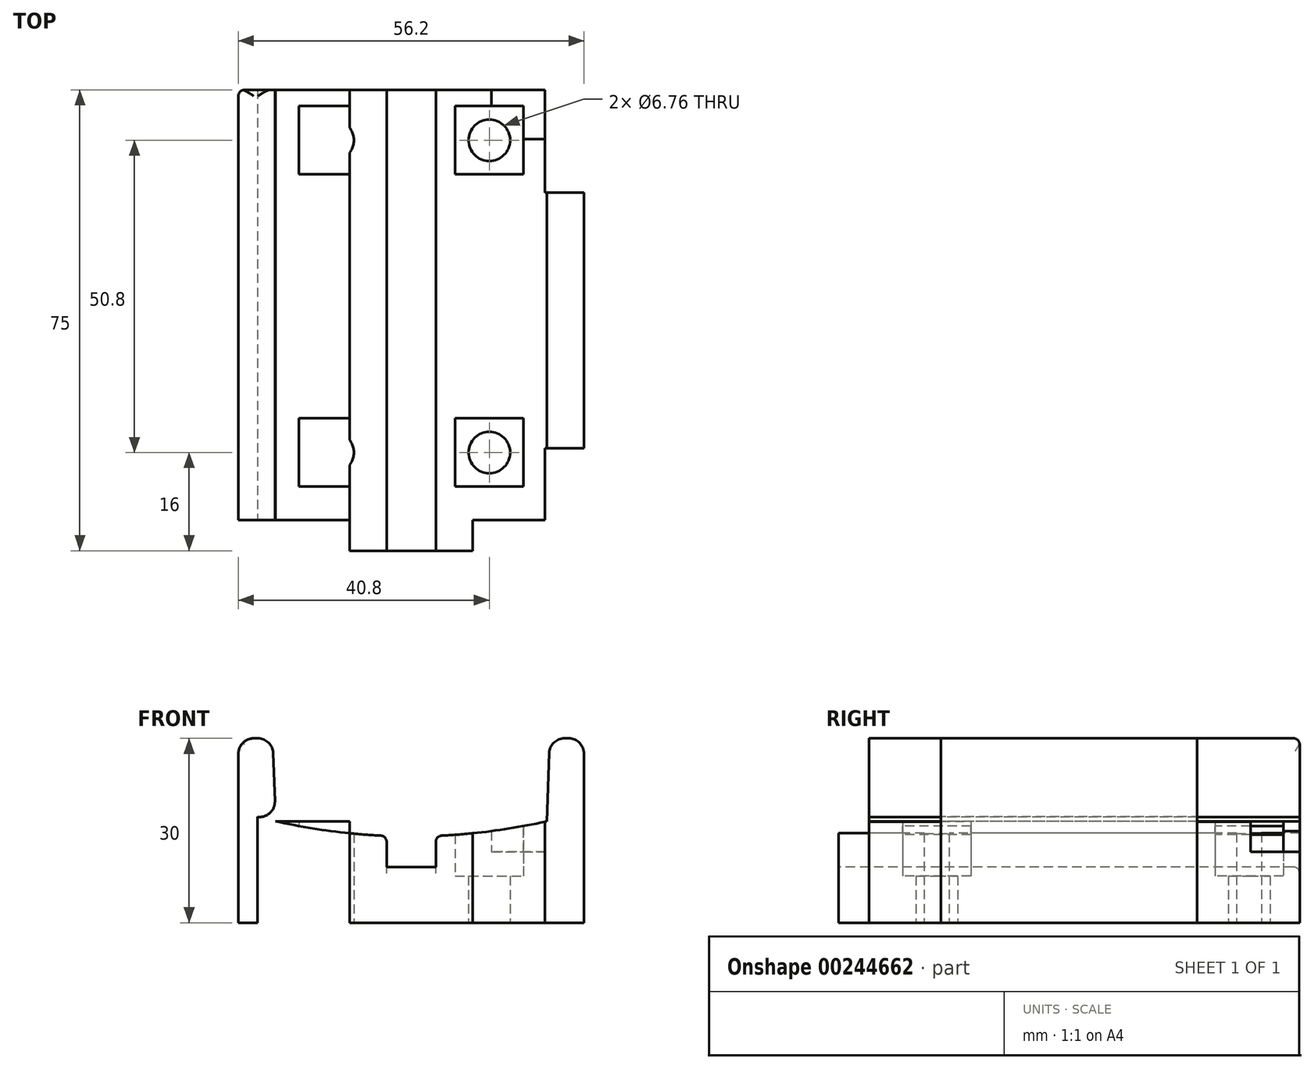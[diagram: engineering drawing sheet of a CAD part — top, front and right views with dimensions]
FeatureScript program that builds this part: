
annotation { "Feature Type Name" : "Feature", "Feature Type Description" : "" }
export const myFeature = defineFeature(function(context is Context, id is Id, definition is map)
    precondition{}
    {
        {
            var Q0;
            Q0=qCreatedBy(makeId("Front.planeOp"),FACE);
            var sketch = newSketch(context, id + "F0", { "sketchPlane" : qUnion([Q0])});
            skCircle(sketch, "E0", {"center": v(0, 0) * mm, "radius": 100.1 * mm});
            skLineSegment(sketch, "E1", {"start": v(0, 0) * mm, "end": v(0, -100.1) * mm});
            skLineSegment(sketch, "E2", {"start": v(0, -97.64) * mm, "end": v(22.05, -97.64) * mm});
            skLineSegment(sketch, "E3", {"start": v(0, -97.64) * mm, "end": v(-22.05, -97.64) * mm});
            skLineSegment(sketch, "E4", {"start": v(0, 0) * mm, "end": v(0, -27.77) * mm});
            skLineSegment(sketch, "E5", {"start": v(0, 0) * mm, "end": v(0, -84.15) * mm});
            skLineSegment(sketch, "E6", {"start": v(0, -84.15) * mm, "end": v(22.52, -84.15) * mm});
            skLineSegment(sketch, "E7", {"start": v(22.52, -84.15) * mm, "end": v(22.05, -97.64) * mm});
            skLineSegment(sketch, "E8", {"start": v(0, -84.15) * mm, "end": v(-22.52, -84.15) * mm});
            skLineSegment(sketch, "E9", {"start": v(-22.52, -84.15) * mm, "end": v(-22.05, -97.64) * mm});
            skLineSegment(sketch, "E10", {"start": v(-22.52, -84.15) * mm, "end": v(-28.1, -84.15) * mm});
            skLineSegment(sketch, "E11", {"start": v(-28.1, -84.15) * mm, "end": v(-28.1, -104.15) * mm});
            skLineSegment(sketch, "E12", {"start": v(-28.1, -104.15) * mm, "end": v(-48.1, -104.15) * mm});
            skLineSegment(sketch, "E13", {"start": v(-48.1, -104.15) * mm, "end": v(-48.1, -114.15) * mm});
            skLineSegment(sketch, "E14", {"start": v(-48.1, -114.15) * mm, "end": v(0, -114.15) * mm});
            skLineSegment(sketch, "E15", {"start": v(0, -114.15) * mm, "end": v(48.1, -114.15) * mm});
            skLineSegment(sketch, "E16", {"start": v(48.1, -114.15) * mm, "end": v(48.1, -104.15) * mm});
            skLineSegment(sketch, "E17", {"start": v(0, -97.64) * mm, "end": v(4, -97.64) * mm});
            skLineSegment(sketch, "E18", {"start": v(4, -105.1) * mm, "end": v(-4, -105.1) * mm});
            skLineSegment(sketch, "E19", {"start": v(-4, -105.1) * mm, "end": v(-4, -97.64) * mm});
            skLineSegment(sketch, "E20", {"start": v(4, -105.1) * mm, "end": v(4, -97.64) * mm});
            skLineSegment(sketch, "E21", {"start": v(22.05, -97.64) * mm, "end": v(13.05, -97.64) * mm});
            skLineSegment(sketch, "E22", {"start": v(13.05, -97.64) * mm, "end": v(13.05, -102.64) * mm});
            skLineSegment(sketch, "E23", {"start": v(13.05, -102.64) * mm, "end": v(22.05, -102.64) * mm});
            skLineSegment(sketch, "E24", {"start": v(22.05, -102.64) * mm, "end": v(22.05, -97.64) * mm});
            skLineSegment(sketch, "E25", {"start": v(22.52, -84.15) * mm, "end": v(28.1, -84.15) * mm});
            skLineSegment(sketch, "E26", {"start": v(28.1, -84.15) * mm, "end": v(28.1, -104.15) * mm});
            skLineSegment(sketch, "E27", {"start": v(28.1, -104.15) * mm, "end": v(48.1, -104.15) * mm});
            skLineSegment(sketch, "E28", {"start": v(-28.1, -104.15) * mm, "end": v(-28.1, -114.15) * mm});
            skLineSegment(sketch, "E29", {"start": v(28.1, -104.15) * mm, "end": v(28.1, -114.15) * mm});
            skLineSegment(sketch, "E30.bottom", {"start": v(-22.52, -84.15) * mm, "end": v(22.52, -84.15) * mm});
            skLineSegment(sketch, "E30.top", {"start": v(-22.52, -114.15) * mm, "end": v(22.52, -114.15) * mm});
            skLineSegment(sketch, "E31", {"start": v(0, -84.15) * mm, "end": v(10, -84.15) * mm});
            skLineSegment(sketch, "E32", {"start": v(10, -84.15) * mm, "end": v(10, -114.15) * mm});
            skLineSegment(sketch, "E33", {"start": v(0, -84.15) * mm, "end": v(-10, -84.15) * mm});
            skLineSegment(sketch, "E34", {"start": v(-10, -84.15) * mm, "end": v(-10, -114.15) * mm});
            skLineSegment(sketch, "E35", {"start": v(-10, -114.15) * mm, "end": v(10, -114.15) * mm});
            skLineSegment(sketch, "E36", {"start": v(0, -114.15) * mm, "end": v(-25, -114.15) * mm});
            skLineSegment(sketch, "E37", {"start": v(-25, -114.15) * mm, "end": v(-25, -84.15) * mm});
            skLineSegment(sketch, "E38", {"start": v(-25, -84.15) * mm, "end": v(0, -84.15) * mm});
            skLineSegment(sketch, "E39", {"start": v(0, -114.15) * mm, "end": v(25, -114.15) * mm});
            skLineSegment(sketch, "E40", {"start": v(25, -114.15) * mm, "end": v(25, -84.15) * mm});
            skPoint(sketch, "E40.endSnap0", {"position": v(25.31, -84.15) * mm});
            skLineSegment(sketch, "E41", {"start": v(25, -84.15) * mm, "end": v(0, -84.15) * mm});
            skSolve(sketch);
        }
        {
            var Q0;
            {var subQ0=sQuery(id+"F0.wireOp",EDGE,"E9");Q0=makeQuery(id+"F0.imprint","IMPRINT",FACE,{"disambiguationData":[TD([[makeQuery(id+"F0.imprint","IMPRINT",EDGE,{"derivedFrom":subQ0}),-1.0]])]});}
            var Q1;
            {var subQ0=sQuery(id+"F0.wireOp",EDGE,"E7");Q1=makeQuery(id+"F0.imprint","IMPRINT",FACE,{"disambiguationData":[TD([[makeQuery(id+"F0.imprint","IMPRINT",EDGE,{"derivedFrom":subQ0}),1.0]])]});}
            var Q2;
            {var subQ4=sQuery(id+"F0.wireOp",EDGE,"E23");Q2=makeQuery(id+"F0.imprint","IMPRINT",FACE,{"disambiguationData":[TD([[makeQuery(id+"F0.imprint","IMPRINT",EDGE,{"derivedFrom":subQ4}),1.0]])]});}
            var Q3;
            {var subQ1=sQuery(id+"F0.wireOp",EDGE,"E18");Q3=makeQuery(id+"F0.imprint","IMPRINT",FACE,{"disambiguationData":[TD([[makeQuery(id+"F0.imprint","IMPRINT",EDGE,{"derivedFrom":subQ1}),1.0]])]});}
            var Q4;
            {var subQ0=sQuery(id+"F0.wireOp",EDGE,"E28");Q4=makeQuery(id+"F0.imprint","IMPRINT",FACE,{"disambiguationData":[TD([[makeQuery(id+"F0.imprint","IMPRINT",EDGE,{"derivedFrom":subQ0}),1.0]])]});}
            var Q5;
            {var subQ0=sQuery(id+"F0.wireOp",EDGE,"E29");Q5=makeQuery(id+"F0.imprint","IMPRINT",FACE,{"disambiguationData":[TD([[makeQuery(id+"F0.imprint","IMPRINT",EDGE,{"derivedFrom":subQ0}),-1.0]])]});}
            var Q6;
            {var subQ5=sQuery(id+"F0.wireOp",EDGE,"E25");Q6=makeQuery(id+"F0.imprint","IMPRINT",FACE,{"disambiguationData":[TD([[makeQuery(id+"F0.imprint","IMPRINT",EDGE,{"derivedFrom":subQ5}),-1.0]])]});}
            var Q7;
            {var subQ5=sQuery(id+"F0.wireOp",EDGE,"E10");Q7=makeQuery(id+"F0.imprint","IMPRINT",FACE,{"disambiguationData":[TD([[makeQuery(id+"F0.imprint","IMPRINT",EDGE,{"derivedFrom":subQ5}),1.0]])]});}
            var Q8;
            {var subQ0=sQuery(id+"F0.wireOp",EDGE,"E23");Q8=makeQuery(id+"F0.imprint","IMPRINT",FACE,{"disambiguationData":[TD([[makeQuery(id+"F0.imprint","IMPRINT",EDGE,{"derivedFrom":subQ0}),-1.0]])]});}
            var Q9;
            {var subQ1=sQuery(id+"F0.wireOp",EDGE,"E36");var subQ3=sQuery(id+"F0.wireOp",EDGE,"E34");var subQ4=makeQuery(id+"F0.imprint","INTERSECT",VERTEX,{"derivedFrom":[subQ3,subQ1]});Q9=makeQuery(id+"F0.imprint","IMPRINT",FACE,{"disambiguationData":[TD([[makeQuery(id+"F0.imprint","IMPRINT",EDGE,{"disambiguationData":[TD([[subQ4,1.0]])],"derivedFrom":subQ3}),-1.0]])]});}
            extrude(context, id + "F1", {"entities" : qUnion([Q0, Q1, Q2, Q3, Q4, Q5, Q6, Q7, Q8, Q9]), "oppositeDirection" : true, "depth" : 75 * mm});
        }
        {
            var Q0;
            Q0=makeQuery(id+"F1.opExtrude","SWEPT_FACE",FACE,{"disambiguationData":[OSD([sQuery(id+"F0.wireOp",EDGE,"E14"),sQuery(id+"F0.wireOp",EDGE,"E15")])]});
            var sketch = newSketch(context, id + "F2", { "sketchPlane" : qUnion([Q0])});
            skLineSegment(sketch, "E42", {"start": v(0, 0) * mm, "end": v(-12.7, 0) * mm});
            skLineSegment(sketch, "E43", {"start": v(-12.7, 0) * mm, "end": v(-25.4, 0) * mm});
            skLineSegment(sketch, "E44", {"start": v(0, 0) * mm, "end": v(12.7, 0) * mm});
            skPoint(sketch, "E45.endSnap0", {"position": v(6.35, 0) * mm});
            skLineSegment(sketch, "E46", {"start": v(-12.7, 0) * mm, "end": v(-12.7, -184.7) * mm});
            skLineSegment(sketch, "E47", {"start": v(12.7, 0) * mm, "end": v(12.7, -185) * mm});
            skLineSegment(sketch, "E48", {"start": v(0, 0) * mm, "end": v(0, -16) * mm});
            skLineSegment(sketch, "E49", {"start": v(0, -16) * mm, "end": v(0, -66.8) * mm});
            skLineSegment(sketch, "E50", {"start": v(0, -66.8) * mm, "end": v(0, -117.6) * mm});
            skLineSegment(sketch, "E51", {"start": v(0, -117.6) * mm, "end": v(0, -168.4) * mm});
            skLineSegment(sketch, "E52", {"start": v(-12.7, -16) * mm, "end": v(12.7, -16) * mm});
            skLineSegment(sketch, "E53", {"start": v(-12.7, -66.8) * mm, "end": v(12.7, -66.8) * mm});
            skLineSegment(sketch, "E54", {"start": v(-12.7, -117.6) * mm, "end": v(12.7, -117.6) * mm});
            skLineSegment(sketch, "E55", {"start": v(-12.7, -168.4) * mm, "end": v(12.7, -168.4) * mm});
            skLineSegment(sketch, "E56", {"start": v(-28.1, -117.9) * mm, "end": v(-28.1, -168.4) * mm});
            skLineSegment(sketch, "E57", {"start": v(-28.1, -15.7) * mm, "end": v(-28.1, -67.1) * mm});
            skLineSegment(sketch, "E58", {"start": v(21.77, -66.7) * mm, "end": v(28.1, -66.7) * mm});
            skLineSegment(sketch, "E59", {"start": v(28.1, -66.7) * mm, "end": v(28.1, -118.3) * mm});
            skLineSegment(sketch, "E60", {"start": v(28.1, -118.3) * mm, "end": v(21.77, -118.3) * mm});
            skLineSegment(sketch, "E61", {"start": v(21.77, -118.3) * mm, "end": v(21.77, -66.7) * mm});
            skLineSegment(sketch, "E62", {"start": v(28.1, -58.3) * mm, "end": v(28.1, -75) * mm});
            skLineSegment(sketch, "E63", {"start": v(28.1, -16.7) * mm, "end": v(21.77, -16.7) * mm});
            skLineSegment(sketch, "E64", {"start": v(28.1, -58.3) * mm, "end": v(21.77, -58.3) * mm});
            skLineSegment(sketch, "E65", {"start": v(21.77, -58.3) * mm, "end": v(21.77, -75) * mm});
            skLineSegment(sketch, "E66", {"start": v(21.77, -75) * mm, "end": v(28.1, -75) * mm});
            skLineSegment(sketch, "E67.bottom", {"start": v(-18.26, -173.96) * mm, "end": v(-7.14, -173.96) * mm});
            skLineSegment(sketch, "E67.top", {"start": v(-18.26, -162.84) * mm, "end": v(-7.14, -162.84) * mm});
            skLineSegment(sketch, "E67.left", {"start": v(-18.26, -173.96) * mm, "end": v(-18.26, -162.84) * mm});
            skLineSegment(sketch, "E67.right", {"start": v(-7.14, -173.96) * mm, "end": v(-7.14, -162.84) * mm});
            skPoint(sketch, "E67.middle", {"position": v(-12.7, -168.4) * mm});
            skLineSegment(sketch, "E68.bottom", {"start": v(7.14, -173.96) * mm, "end": v(18.26, -173.96) * mm});
            skLineSegment(sketch, "E68.top", {"start": v(7.14, -162.84) * mm, "end": v(18.26, -162.84) * mm});
            skLineSegment(sketch, "E68.left", {"start": v(7.14, -173.96) * mm, "end": v(7.14, -162.84) * mm});
            skLineSegment(sketch, "E68.right", {"start": v(18.26, -173.96) * mm, "end": v(18.26, -162.84) * mm});
            skPoint(sketch, "E68.middle", {"position": v(12.7, -168.4) * mm});
            skLineSegment(sketch, "E69.bottom", {"start": v(7.14, -123.16) * mm, "end": v(18.26, -123.16) * mm});
            skLineSegment(sketch, "E69.top", {"start": v(7.14, -112.04) * mm, "end": v(18.26, -112.04) * mm});
            skLineSegment(sketch, "E69.left", {"start": v(7.14, -123.16) * mm, "end": v(7.14, -112.04) * mm});
            skLineSegment(sketch, "E69.right", {"start": v(18.26, -123.16) * mm, "end": v(18.26, -112.04) * mm});
            skPoint(sketch, "E69.middle", {"position": v(12.7, -117.6) * mm});
            skLineSegment(sketch, "E70.bottom", {"start": v(-18.26, -123.16) * mm, "end": v(-7.14, -123.16) * mm});
            skLineSegment(sketch, "E70.top", {"start": v(-18.26, -112.04) * mm, "end": v(-7.14, -112.04) * mm});
            skLineSegment(sketch, "E70.left", {"start": v(-18.26, -123.16) * mm, "end": v(-18.26, -112.04) * mm});
            skLineSegment(sketch, "E70.right", {"start": v(-7.14, -123.16) * mm, "end": v(-7.14, -112.04) * mm});
            skPoint(sketch, "E70.middle", {"position": v(-12.7, -117.6) * mm});
            skLineSegment(sketch, "E71.bottom", {"start": v(7.14, -72.36) * mm, "end": v(18.26, -72.36) * mm});
            skLineSegment(sketch, "E71.top", {"start": v(7.14, -61.24) * mm, "end": v(18.26, -61.24) * mm});
            skLineSegment(sketch, "E71.left", {"start": v(7.14, -72.36) * mm, "end": v(7.14, -61.24) * mm});
            skLineSegment(sketch, "E71.right", {"start": v(18.26, -72.36) * mm, "end": v(18.26, -61.24) * mm});
            skPoint(sketch, "E71.middle", {"position": v(12.7, -66.8) * mm});
            skLineSegment(sketch, "E72.bottom", {"start": v(-18.26, -72.36) * mm, "end": v(-7.14, -72.36) * mm});
            skLineSegment(sketch, "E72.top", {"start": v(-18.26, -61.24) * mm, "end": v(-7.14, -61.24) * mm});
            skLineSegment(sketch, "E72.left", {"start": v(-18.26, -72.36) * mm, "end": v(-18.26, -61.24) * mm});
            skLineSegment(sketch, "E72.right", {"start": v(-7.14, -72.36) * mm, "end": v(-7.14, -61.24) * mm});
            skPoint(sketch, "E72.middle", {"position": v(-12.7, -66.8) * mm});
            skLineSegment(sketch, "E73.bottom", {"start": v(7.14, -21.56) * mm, "end": v(18.26, -21.56) * mm});
            skLineSegment(sketch, "E73.top", {"start": v(7.14, -10.44) * mm, "end": v(18.26, -10.44) * mm});
            skLineSegment(sketch, "E73.left", {"start": v(7.14, -21.56) * mm, "end": v(7.14, -10.44) * mm});
            skLineSegment(sketch, "E73.right", {"start": v(18.26, -21.56) * mm, "end": v(18.26, -10.44) * mm});
            skPoint(sketch, "E73.middle", {"position": v(12.7, -16) * mm});
            skLineSegment(sketch, "E74.bottom", {"start": v(-18.26, -21.56) * mm, "end": v(-7.14, -21.56) * mm});
            skLineSegment(sketch, "E74.top", {"start": v(-18.26, -10.44) * mm, "end": v(-7.14, -10.44) * mm});
            skLineSegment(sketch, "E74.left", {"start": v(-18.26, -21.56) * mm, "end": v(-18.26, -10.44) * mm});
            skLineSegment(sketch, "E74.right", {"start": v(-7.14, -21.56) * mm, "end": v(-7.14, -10.44) * mm});
            skPoint(sketch, "E74.middle", {"position": v(-12.7, -16) * mm});
            skLineSegment(sketch, "E75", {"start": v(-28.1, -67.1) * mm, "end": v(-21.77, -67.1) * mm});
            skLineSegment(sketch, "E76", {"start": v(-21.77, -67.1) * mm, "end": v(-21.77, -15.7) * mm});
            skLineSegment(sketch, "E77", {"start": v(-21.77, -15.7) * mm, "end": v(-28.1, -15.7) * mm});
            skLineSegment(sketch, "E78", {"start": v(-28.1, -168.4) * mm, "end": v(-21.77, -168.4) * mm});
            skLineSegment(sketch, "E79", {"start": v(-21.77, -168.4) * mm, "end": v(-21.77, -117.9) * mm});
            skLineSegment(sketch, "E80", {"start": v(-21.77, -117.9) * mm, "end": v(-28.1, -117.9) * mm});
            skLineSegment(sketch, "E81", {"start": v(-21.77, -67.1) * mm, "end": v(-21.77, -59.3) * mm});
            skLineSegment(sketch, "E82", {"start": v(-21.77, -59.3) * mm, "end": v(-28.1, -59.3) * mm});
            skLineSegment(sketch, "E83", {"start": v(-28.1, -59.3) * mm, "end": v(-28.1, -67.1) * mm});
            skLineSegment(sketch, "E84", {"start": v(21.77, -16.7) * mm, "end": v(21.77, 0.7) * mm});
            skLineSegment(sketch, "E85", {"start": v(21.77, 0.7) * mm, "end": v(28.1, 0.7) * mm});
            skLineSegment(sketch, "E86", {"start": v(28.1, 0.7) * mm, "end": v(28.1, -16.7) * mm});
            skSolve(sketch);
        }
        {
            var Q0;
            {var subQ4=sQuery(id+"F0.wireOp",EDGE,"E23");Q0=makeQuery(id+"F0.imprint","IMPRINT",FACE,{"disambiguationData":[TD([[makeQuery(id+"F0.imprint","IMPRINT",EDGE,{"derivedFrom":subQ4}),1.0]])]});}
            extrude(context, id + "F3", {"entities" : qUnion([Q0]), "operationType" : NewBodyOperationType.REMOVE, "endBound" : BoundingType.UP_TO_NEXT, "oppositeDirection" : true, "depth" : 30 * mm, "hasSecondDirection" : true, "secondDirectionOppositeDirection" : true, "secondDirectionDepth" : 67 * mm});
        }
        {
            var Q0;
            Q0=sQuery(id+"F2.wireOp",VERTEX,"E55.start");
            var Q1;
            Q1=sQuery(id+"F2.wireOp",VERTEX,"E55.end");
            var Q2;
            Q2=sQuery(id+"F2.wireOp",VERTEX,"E54.start");
            var Q3;
            Q3=sQuery(id+"F2.wireOp",VERTEX,"E54.end");
            var Q4;
            Q4=sQuery(id+"F2.wireOp",VERTEX,"E53.start");
            var Q5;
            Q5=sQuery(id+"F2.wireOp",VERTEX,"E53.end");
            var Q6;
            Q6=sQuery(id+"F2.wireOp",VERTEX,"E52.start");
            var Q7;
            Q7=sQuery(id+"F2.wireOp",VERTEX,"E52.end");
            var Q8;
            Q8=makeQuery(id+"F1.opExtrude","SWEPT_BODY",BODY,{"disambiguationData":[OSD([sQuery(id+"F0.wireOp",EDGE,"E0"),sQuery(id+"F0.wireOp",EDGE,"E7"),sQuery(id+"F0.wireOp",EDGE,"E9"),sQuery(id+"F0.wireOp",EDGE,"E10"),sQuery(id+"F0.wireOp",EDGE,"E11"),sQuery(id+"F0.wireOp",EDGE,"E14"),sQuery(id+"F0.wireOp",EDGE,"E15"),sQuery(id+"F0.wireOp",EDGE,"E18"),sQuery(id+"F0.wireOp",EDGE,"E19"),sQuery(id+"F0.wireOp",EDGE,"E20"),sQuery(id+"F0.wireOp",EDGE,"E25"),sQuery(id+"F0.wireOp",EDGE,"E26"),sQuery(id+"F0.wireOp",EDGE,"E28"),sQuery(id+"F0.wireOp",EDGE,"E29")])]});
            hole(context, id + "F4", {"style" : HoleStyle.SIMPLE, "endStyle" : HoleEndStyle.THROUGH, "standardTappedOrClearance" : lookupTablePath({ "standard" : "ANSI", "fit" : "Normal (ASME)", "size" : "1/4", "type" : "Clearance" }), "standardBlindInLast" : lookupTablePath({ "fit" : "Free", "standard" : "ANSI", "size" : "1/4", "type" : "Clearance" }), "holeDiameter" : 6.76 * mm, "tappedDepth" : 12 * mm, "tapClearance" : 3, "locations" : qUnion([Q0, Q1, Q2, Q3, Q4, Q5, Q6, Q7]), "scope" : qUnion([Q8])});
        }
        {
            var Q0;
            {var subQ0=sQuery(id+"F2.wireOp",EDGE,"E67.left");Q0=makeQuery(id+"F2.imprint","IMPRINT",FACE,{"disambiguationData":[TD([[makeQuery(id+"F2.imprint","IMPRINT",EDGE,{"derivedFrom":subQ0}),-1.0]])]});}
            var Q1;
            {var subQ0=sQuery(id+"F2.wireOp",EDGE,"E55");var subQ1=sQuery(id+"F2.wireOp",EDGE,"E46");var subQ2=makeQuery(id+"F2.imprint","INTERSECT",VERTEX,{"derivedFrom":[subQ1,subQ0]});Q1=makeQuery(id+"F2.imprint","IMPRINT",FACE,{"disambiguationData":[TD([[makeQuery(id+"F2.imprint","IMPRINT",EDGE,{"disambiguationData":[TD([[subQ2,1.0]])],"derivedFrom":subQ1}),1.0]])]});}
            var Q2;
            {var subQ0=sQuery(id+"F2.wireOp",EDGE,"E55");var subQ1=sQuery(id+"F2.wireOp",EDGE,"E46");var subQ2=makeQuery(id+"F2.imprint","INTERSECT",VERTEX,{"derivedFrom":[subQ1,subQ0]});Q2=makeQuery(id+"F2.imprint","IMPRINT",FACE,{"disambiguationData":[TD([[makeQuery(id+"F2.imprint","IMPRINT",EDGE,{"disambiguationData":[TD([[subQ2,-1.0]])],"derivedFrom":subQ1}),1.0]])]});}
            var Q3;
            {var subQ0=sQuery(id+"F2.wireOp",EDGE,"E55");var subQ1=sQuery(id+"F2.wireOp",EDGE,"E47");var subQ2=makeQuery(id+"F2.imprint","INTERSECT",VERTEX,{"derivedFrom":[subQ1,subQ0]});Q3=makeQuery(id+"F2.imprint","IMPRINT",FACE,{"disambiguationData":[TD([[makeQuery(id+"F2.imprint","IMPRINT",EDGE,{"disambiguationData":[TD([[subQ2,-1.0]])],"derivedFrom":subQ1}),-1.0]])]});}
            var Q4;
            {var subQ0=sQuery(id+"F2.wireOp",EDGE,"E55");var subQ1=sQuery(id+"F2.wireOp",EDGE,"E47");var subQ2=makeQuery(id+"F2.imprint","INTERSECT",VERTEX,{"derivedFrom":[subQ1,subQ0]});Q4=makeQuery(id+"F2.imprint","IMPRINT",FACE,{"disambiguationData":[TD([[makeQuery(id+"F2.imprint","IMPRINT",EDGE,{"disambiguationData":[TD([[subQ2,1.0]])],"derivedFrom":subQ1}),-1.0]])]});}
            var Q5;
            {var subQ0=sQuery(id+"F2.wireOp",EDGE,"E68.right");Q5=makeQuery(id+"F2.imprint","IMPRINT",FACE,{"disambiguationData":[TD([[makeQuery(id+"F2.imprint","IMPRINT",EDGE,{"derivedFrom":subQ0}),1.0]])]});}
            var Q6;
            {var subQ0=sQuery(id+"F2.wireOp",EDGE,"E69.right");Q6=makeQuery(id+"F2.imprint","IMPRINT",FACE,{"disambiguationData":[TD([[makeQuery(id+"F2.imprint","IMPRINT",EDGE,{"derivedFrom":subQ0}),1.0]])]});}
            var Q7;
            {var subQ0=sQuery(id+"F2.wireOp",EDGE,"E54");var subQ1=sQuery(id+"F2.wireOp",EDGE,"E47");var subQ2=makeQuery(id+"F2.imprint","INTERSECT",VERTEX,{"derivedFrom":[subQ1,subQ0]});Q7=makeQuery(id+"F2.imprint","IMPRINT",FACE,{"disambiguationData":[TD([[makeQuery(id+"F2.imprint","IMPRINT",EDGE,{"disambiguationData":[TD([[subQ2,1.0]])],"derivedFrom":subQ1}),-1.0]])]});}
            var Q8;
            {var subQ0=sQuery(id+"F2.wireOp",EDGE,"E54");var subQ1=sQuery(id+"F2.wireOp",EDGE,"E47");var subQ2=makeQuery(id+"F2.imprint","INTERSECT",VERTEX,{"derivedFrom":[subQ1,subQ0]});Q8=makeQuery(id+"F2.imprint","IMPRINT",FACE,{"disambiguationData":[TD([[makeQuery(id+"F2.imprint","IMPRINT",EDGE,{"disambiguationData":[TD([[subQ2,-1.0]])],"derivedFrom":subQ1}),-1.0]])]});}
            var Q9;
            {var subQ0=sQuery(id+"F2.wireOp",EDGE,"E54");var subQ1=sQuery(id+"F2.wireOp",EDGE,"E46");var subQ2=makeQuery(id+"F2.imprint","INTERSECT",VERTEX,{"derivedFrom":[subQ1,subQ0]});Q9=makeQuery(id+"F2.imprint","IMPRINT",FACE,{"disambiguationData":[TD([[makeQuery(id+"F2.imprint","IMPRINT",EDGE,{"disambiguationData":[TD([[subQ2,-1.0]])],"derivedFrom":subQ1}),1.0]])]});}
            var Q10;
            {var subQ0=sQuery(id+"F2.wireOp",EDGE,"E54");var subQ1=sQuery(id+"F2.wireOp",EDGE,"E46");var subQ2=makeQuery(id+"F2.imprint","INTERSECT",VERTEX,{"derivedFrom":[subQ1,subQ0]});Q10=makeQuery(id+"F2.imprint","IMPRINT",FACE,{"disambiguationData":[TD([[makeQuery(id+"F2.imprint","IMPRINT",EDGE,{"disambiguationData":[TD([[subQ2,1.0]])],"derivedFrom":subQ1}),1.0]])]});}
            var Q11;
            {var subQ0=sQuery(id+"F2.wireOp",EDGE,"E70.left");Q11=makeQuery(id+"F2.imprint","IMPRINT",FACE,{"disambiguationData":[TD([[makeQuery(id+"F2.imprint","IMPRINT",EDGE,{"derivedFrom":subQ0}),-1.0]])]});}
            var Q12;
            {var subQ0=sQuery(id+"F2.wireOp",EDGE,"E53");var subQ1=sQuery(id+"F2.wireOp",EDGE,"E46");var subQ2=makeQuery(id+"F2.imprint","INTERSECT",VERTEX,{"derivedFrom":[subQ1,subQ0]});Q12=makeQuery(id+"F2.imprint","IMPRINT",FACE,{"disambiguationData":[TD([[makeQuery(id+"F2.imprint","IMPRINT",EDGE,{"disambiguationData":[TD([[subQ2,1.0]])],"derivedFrom":subQ1}),1.0]])]});}
            var Q13;
            {var subQ0=sQuery(id+"F2.wireOp",EDGE,"E53");var subQ1=sQuery(id+"F2.wireOp",EDGE,"E46");var subQ2=makeQuery(id+"F2.imprint","INTERSECT",VERTEX,{"derivedFrom":[subQ1,subQ0]});Q13=makeQuery(id+"F2.imprint","IMPRINT",FACE,{"disambiguationData":[TD([[makeQuery(id+"F2.imprint","IMPRINT",EDGE,{"disambiguationData":[TD([[subQ2,-1.0]])],"derivedFrom":subQ1}),1.0]])]});}
            var Q14;
            {var subQ0=sQuery(id+"F2.wireOp",EDGE,"E72.left");Q14=makeQuery(id+"F2.imprint","IMPRINT",FACE,{"disambiguationData":[TD([[makeQuery(id+"F2.imprint","IMPRINT",EDGE,{"derivedFrom":subQ0}),-1.0]])]});}
            var Q15;
            {var subQ0=sQuery(id+"F2.wireOp",EDGE,"E53");var subQ1=sQuery(id+"F2.wireOp",EDGE,"E47");var subQ2=makeQuery(id+"F2.imprint","INTERSECT",VERTEX,{"derivedFrom":[subQ1,subQ0]});Q15=makeQuery(id+"F2.imprint","IMPRINT",FACE,{"disambiguationData":[TD([[makeQuery(id+"F2.imprint","IMPRINT",EDGE,{"disambiguationData":[TD([[subQ2,1.0]])],"derivedFrom":subQ1}),-1.0]])]});}
            var Q16;
            {var subQ0=sQuery(id+"F2.wireOp",EDGE,"E53");var subQ1=sQuery(id+"F2.wireOp",EDGE,"E47");var subQ2=makeQuery(id+"F2.imprint","INTERSECT",VERTEX,{"derivedFrom":[subQ1,subQ0]});Q16=makeQuery(id+"F2.imprint","IMPRINT",FACE,{"disambiguationData":[TD([[makeQuery(id+"F2.imprint","IMPRINT",EDGE,{"disambiguationData":[TD([[subQ2,-1.0]])],"derivedFrom":subQ1}),-1.0]])]});}
            var Q17;
            {var subQ0=sQuery(id+"F2.wireOp",EDGE,"E71.right");Q17=makeQuery(id+"F2.imprint","IMPRINT",FACE,{"disambiguationData":[TD([[makeQuery(id+"F2.imprint","IMPRINT",EDGE,{"derivedFrom":subQ0}),1.0]])]});}
            var Q18;
            {var subQ0=sQuery(id+"F2.wireOp",EDGE,"E52");var subQ1=sQuery(id+"F2.wireOp",EDGE,"E47");var subQ2=makeQuery(id+"F2.imprint","INTERSECT",VERTEX,{"derivedFrom":[subQ1,subQ0]});Q18=makeQuery(id+"F2.imprint","IMPRINT",FACE,{"disambiguationData":[TD([[makeQuery(id+"F2.imprint","IMPRINT",EDGE,{"disambiguationData":[TD([[subQ2,-1.0]])],"derivedFrom":subQ1}),-1.0]])]});}
            var Q19;
            {var subQ0=sQuery(id+"F2.wireOp",EDGE,"E52");var subQ1=sQuery(id+"F2.wireOp",EDGE,"E47");var subQ2=makeQuery(id+"F2.imprint","INTERSECT",VERTEX,{"derivedFrom":[subQ1,subQ0]});Q19=makeQuery(id+"F2.imprint","IMPRINT",FACE,{"disambiguationData":[TD([[makeQuery(id+"F2.imprint","IMPRINT",EDGE,{"disambiguationData":[TD([[subQ2,1.0]])],"derivedFrom":subQ1}),-1.0]])]});}
            var Q20;
            {var subQ0=sQuery(id+"F2.wireOp",EDGE,"E73.right");Q20=makeQuery(id+"F2.imprint","IMPRINT",FACE,{"disambiguationData":[TD([[makeQuery(id+"F2.imprint","IMPRINT",EDGE,{"derivedFrom":subQ0}),1.0]])]});}
            var Q21;
            {var subQ0=sQuery(id+"F2.wireOp",EDGE,"E52");var subQ1=sQuery(id+"F2.wireOp",EDGE,"E46");var subQ2=makeQuery(id+"F2.imprint","INTERSECT",VERTEX,{"derivedFrom":[subQ1,subQ0]});Q21=makeQuery(id+"F2.imprint","IMPRINT",FACE,{"disambiguationData":[TD([[makeQuery(id+"F2.imprint","IMPRINT",EDGE,{"disambiguationData":[TD([[subQ2,1.0]])],"derivedFrom":subQ1}),1.0]])]});}
            var Q22;
            {var subQ0=sQuery(id+"F2.wireOp",EDGE,"E74.left");Q22=makeQuery(id+"F2.imprint","IMPRINT",FACE,{"disambiguationData":[TD([[makeQuery(id+"F2.imprint","IMPRINT",EDGE,{"derivedFrom":subQ0}),-1.0]])]});}
            var Q23;
            {var subQ0=sQuery(id+"F2.wireOp",EDGE,"E52");var subQ1=sQuery(id+"F2.wireOp",EDGE,"E46");var subQ2=makeQuery(id+"F2.imprint","INTERSECT",VERTEX,{"derivedFrom":[subQ1,subQ0]});Q23=makeQuery(id+"F2.imprint","IMPRINT",FACE,{"disambiguationData":[TD([[makeQuery(id+"F2.imprint","IMPRINT",EDGE,{"disambiguationData":[TD([[subQ2,-1.0]])],"derivedFrom":subQ1}),1.0]])]});}
            extrude(context, id + "F5", {"entities" : qUnion([Q0, Q1, Q2, Q3, Q4, Q5, Q6, Q7, Q8, Q9, Q10, Q11, Q12, Q13, Q14, Q15, Q16, Q17, Q18, Q19, Q20, Q21, Q22, Q23]), "operationType" : NewBodyOperationType.REMOVE, "endBound" : BoundingType.THROUGH_ALL, "oppositeDirection" : true, "depth" : 15 * mm, "hasSecondDirection" : true, "secondDirectionOppositeDirection" : true, "secondDirectionDepth" : 7.6 * mm});
        }
        {
            var Q0;
            {var subQ0=sQuery(id+"F2.wireOp",EDGE,"E58");Q0=makeQuery(id+"F2.imprint","IMPRINT",FACE,{"disambiguationData":[TD([[makeQuery(id+"F2.imprint","IMPRINT",EDGE,{"derivedFrom":subQ0}),-1.0]])]});}
            var Q1;
            {var subQ0=sQuery(id+"F2.wireOp",EDGE,"E58");Q1=makeQuery(id+"F2.imprint","IMPRINT",FACE,{"disambiguationData":[TD([[makeQuery(id+"F2.imprint","IMPRINT",EDGE,{"derivedFrom":subQ0}),-1.0]])]});}
            var Q2;
            Q2=makeQuery(id+"F2.imprint","IMPRINT",FACE,{"disambiguationData":[TD([[makeQuery(id+"F2.imprint","IMPRINT",EDGE,{"derivedFrom":sQuery(id+"F2.wireOp",EDGE,"a3CpeP2F-AtSb-YDeI-LV00-WMkljdctUo1Q")}),1.0]])]});
            var Q3;
            Q3=makeQuery(id+"F2.imprint","IMPRINT",FACE,{"disambiguationData":[TD([[makeQuery(id+"F2.imprint","IMPRINT",EDGE,{"derivedFrom":sQuery(id+"F2.wireOp",EDGE,"E57")}),-1.0]])]});
            var Q4;
            {var subQ0=sQuery(id+"F2.wireOp",EDGE,"E58");Q4=makeQuery(id+"F2.imprint","IMPRINT",FACE,{"disambiguationData":[TD([[makeQuery(id+"F2.imprint","IMPRINT",EDGE,{"derivedFrom":subQ0}),1.0]])]});}
            var Q5;
            {var subQ0=sQuery(id+"F2.wireOp",EDGE,"E63");Q5=makeQuery(id+"F2.imprint","IMPRINT",FACE,{"disambiguationData":[TD([[makeQuery(id+"F2.imprint","IMPRINT",EDGE,{"derivedFrom":subQ0}),-1.0]])]});}
            var Q6;
            {var subQ0=sQuery(id+"F2.wireOp",EDGE,"E85");Q6=makeQuery(id+"F2.imprint","IMPRINT",FACE,{"disambiguationData":[TD([[makeQuery(id+"F2.imprint","IMPRINT",EDGE,{"derivedFrom":subQ0}),-1.0]])]});}
            extrude(context, id + "F6", {"entities" : qUnion([Q0, Q1, Q2, Q3, Q4, Q5, Q6]), "operationType" : NewBodyOperationType.REMOVE, "endBound" : BoundingType.UP_TO_NEXT, "oppositeDirection" : true, "depth" : 30 * mm});
        }
        {
            var Q0;
            Q0=makeQuery(id+"F1.opExtrude","CAP_EDGE",EDGE,{"disambiguationData":[OSD([sQuery(id+"F0.wireOp",EDGE,"E11"),sQuery(id+"F0.wireOp",EDGE,"E28")])],"isStart":false});
            var Q1;
            Q1=makeQuery(id+"FL0RJ68rYM0qjLv_1.opExtrude","CAP_EDGE",EDGE,{"disambiguationData":[OSD([sQuery(id+"F0.wireOp",EDGE,"E40")])],"isStart":true});
            var Q2;
            Q2=makeQuery(id+"F1.opExtrude","SWEPT_EDGE",EDGE,{"disambiguationData":[OSD([sQuery(id+"F0.wireOp",EDGE,"E0"),sQuery(id+"F0.wireOp",EDGE,"E19")])]});
            var Q3;
            Q3=makeQuery(id+"F1.opExtrude","SWEPT_EDGE",EDGE,{"disambiguationData":[OSD([sQuery(id+"F0.wireOp",EDGE,"E0"),sQuery(id+"F0.wireOp",EDGE,"E20")])]});
            var Q4;
            Q4=makeQuery(id+"F1.opExtrude","CAP_EDGE",EDGE,{"disambiguationData":[OSD([sQuery(id+"F0.wireOp",EDGE,"E18")])],"isStart":false});
            var Q5;
            Q5=makeQuery(id+"FL0RJ68rYM0qjLv_1.opExtrude","CAP_EDGE",EDGE,{"disambiguationData":[OSD([sQuery(id+"F0.wireOp",EDGE,"E41")])],"isStart":false});
            var Q6;
            Q6=makeQuery(id+"FL0RJ68rYM0qjLv_1.opExtrude","CAP_EDGE",EDGE,{"disambiguationData":[OSD([sQuery(id+"F0.wireOp",EDGE,"E38")])],"isStart":false});
            var Q7;
            Q7=makeQuery(id+"F1.opExtrude","CAP_EDGE",EDGE,{"disambiguationData":[OSD([sQuery(id+"F0.wireOp",EDGE,"E10"),sQuery(id+"F0.wireOp",EDGE,"E38")])],"isStart":false});
            fillet(context, id + "F7", {"entities" : qUnion([Q0, Q1, Q2, Q3, Q4, Q5, Q6, Q7]), "radius" : 1 * mm, "tangentPropagation" : true, "allowEdgeOverflow" : false});
        }
        {
            var Q0;
            {var subQ1=sQuery(id+"F0.wireOp",EDGE,"E36");var subQ3=sQuery(id+"F0.wireOp",EDGE,"E34");var subQ4=makeQuery(id+"F0.imprint","INTERSECT",VERTEX,{"derivedFrom":[subQ3,subQ1]});Q0=makeQuery(id+"F0.imprint","IMPRINT",FACE,{"disambiguationData":[TD([[makeQuery(id+"F0.imprint","IMPRINT",EDGE,{"disambiguationData":[TD([[subQ4,1.0]])],"derivedFrom":subQ3}),-1.0]])]});}
            var Q1;
            {var subQ0=sQuery(id+"F0.wireOp",EDGE,"E23");Q1=makeQuery(id+"F0.imprint","IMPRINT",FACE,{"disambiguationData":[TD([[makeQuery(id+"F0.imprint","IMPRINT",EDGE,{"derivedFrom":subQ0}),-1.0]])]});}
            var Q2;
            {var subQ4=sQuery(id+"F0.wireOp",EDGE,"E23");Q2=makeQuery(id+"F0.imprint","IMPRINT",FACE,{"disambiguationData":[TD([[makeQuery(id+"F0.imprint","IMPRINT",EDGE,{"derivedFrom":subQ4}),1.0]])]});}
            var Q3;
            {var subQ0=sQuery(id+"F0.wireOp",EDGE,"E28");Q3=makeQuery(id+"F0.imprint","IMPRINT",FACE,{"disambiguationData":[TD([[makeQuery(id+"F0.imprint","IMPRINT",EDGE,{"derivedFrom":subQ0}),1.0]])]});}
            var Q4;
            {var subQ5=sQuery(id+"F0.wireOp",EDGE,"E10");Q4=makeQuery(id+"F0.imprint","IMPRINT",FACE,{"disambiguationData":[TD([[makeQuery(id+"F0.imprint","IMPRINT",EDGE,{"derivedFrom":subQ5}),1.0]])]});}
            var Q5;
            {var subQ0=sQuery(id+"F0.wireOp",EDGE,"E9");Q5=makeQuery(id+"F0.imprint","IMPRINT",FACE,{"disambiguationData":[TD([[makeQuery(id+"F0.imprint","IMPRINT",EDGE,{"derivedFrom":subQ0}),-1.0]])]});}
            extrude(context, id + "F8", {"entities" : qUnion([Q0, Q1, Q2, Q3, Q4, Q5]), "operationType" : NewBodyOperationType.REMOVE, "oppositeDirection" : true, "depth" : 5 * mm});
        }
        {
            var Q0;
            {var subQ2=sQuery(id+"F0.wireOp",EDGE,"E11");var subQ3=sQuery(id+"F0.wireOp",EDGE,"E10");Q0=makeQuery(id+"F6.boolean.opBoolean","SPLIT",EDGE,{"disambiguationData":[TD([makeQuery(id+"F6.opExtrude","SWEPT_FACE",FACE,{"disambiguationData":[OSD([sQuery(id+"F2.wireOp",EDGE,"E77")])]})])],"derivedFrom":makeQuery(id+"F1.opExtrude","SWEPT_EDGE",EDGE,{"disambiguationData":[OSD([subQ3,subQ2])]})});}
            var Q1;
            {var subQ0=sQuery(id+"F0.wireOp",EDGE,"E38");var subQ2=sQuery(id+"F0.wireOp",EDGE,"E9");Q1=makeQuery(id+"F6.boolean.opBoolean","SPLIT",EDGE,{"disambiguationData":[TD([makeQuery(id+"F6.opExtrude","SWEPT_FACE",FACE,{"disambiguationData":[OSD([sQuery(id+"F2.wireOp",EDGE,"E77")])]})])],"derivedFrom":makeQuery(id+"F1.opExtrude","SWEPT_EDGE",EDGE,{"disambiguationData":[OSD([subQ2,subQ0])]})});}
            var Q2;
            {var subQ2=sQuery(id+"F0.wireOp",EDGE,"E11");var subQ3=sQuery(id+"F0.wireOp",EDGE,"E10");Q2=makeQuery(id+"F6.boolean.opBoolean","SPLIT",EDGE,{"disambiguationData":[TD([makeQuery(id+"F6.opExtrude","SWEPT_FACE",FACE,{"disambiguationData":[OSD([sQuery(id+"F2.wireOp",EDGE,"E82")])]})])],"derivedFrom":makeQuery(id+"F1.opExtrude","SWEPT_EDGE",EDGE,{"disambiguationData":[OSD([subQ3,subQ2])]})});}
            var Q3;
            {var subQ0=sQuery(id+"F0.wireOp",EDGE,"E38");var subQ2=sQuery(id+"F0.wireOp",EDGE,"E9");Q3=makeQuery(id+"F6.boolean.opBoolean","SPLIT",EDGE,{"disambiguationData":[TD([makeQuery(id+"F6.opExtrude","SWEPT_FACE",FACE,{"disambiguationData":[OSD([sQuery(id+"F2.wireOp",EDGE,"E82")])]})])],"derivedFrom":makeQuery(id+"F1.opExtrude","SWEPT_EDGE",EDGE,{"disambiguationData":[OSD([subQ2,subQ0])]})});}
            var Q4;
            Q4=makeQuery(id+"F1.opExtrude","SWEPT_EDGE",EDGE,{"disambiguationData":[OSD([sQuery(id+"F0.wireOp",EDGE,"E7"),sQuery(id+"F0.wireOp",EDGE,"E41")])]});
            var Q5;
            Q5=makeQuery(id+"F1.opExtrude","SWEPT_EDGE",EDGE,{"disambiguationData":[OSD([sQuery(id+"F0.wireOp",EDGE,"E25"),sQuery(id+"F0.wireOp",EDGE,"E26")])]});
            fillet(context, id + "F9", {"entities" : qUnion([Q0, Q1, Q2, Q3, Q4, Q5]), "radius" : 2.5 * mm, "allowEdgeOverflow" : false});
        }
    });
